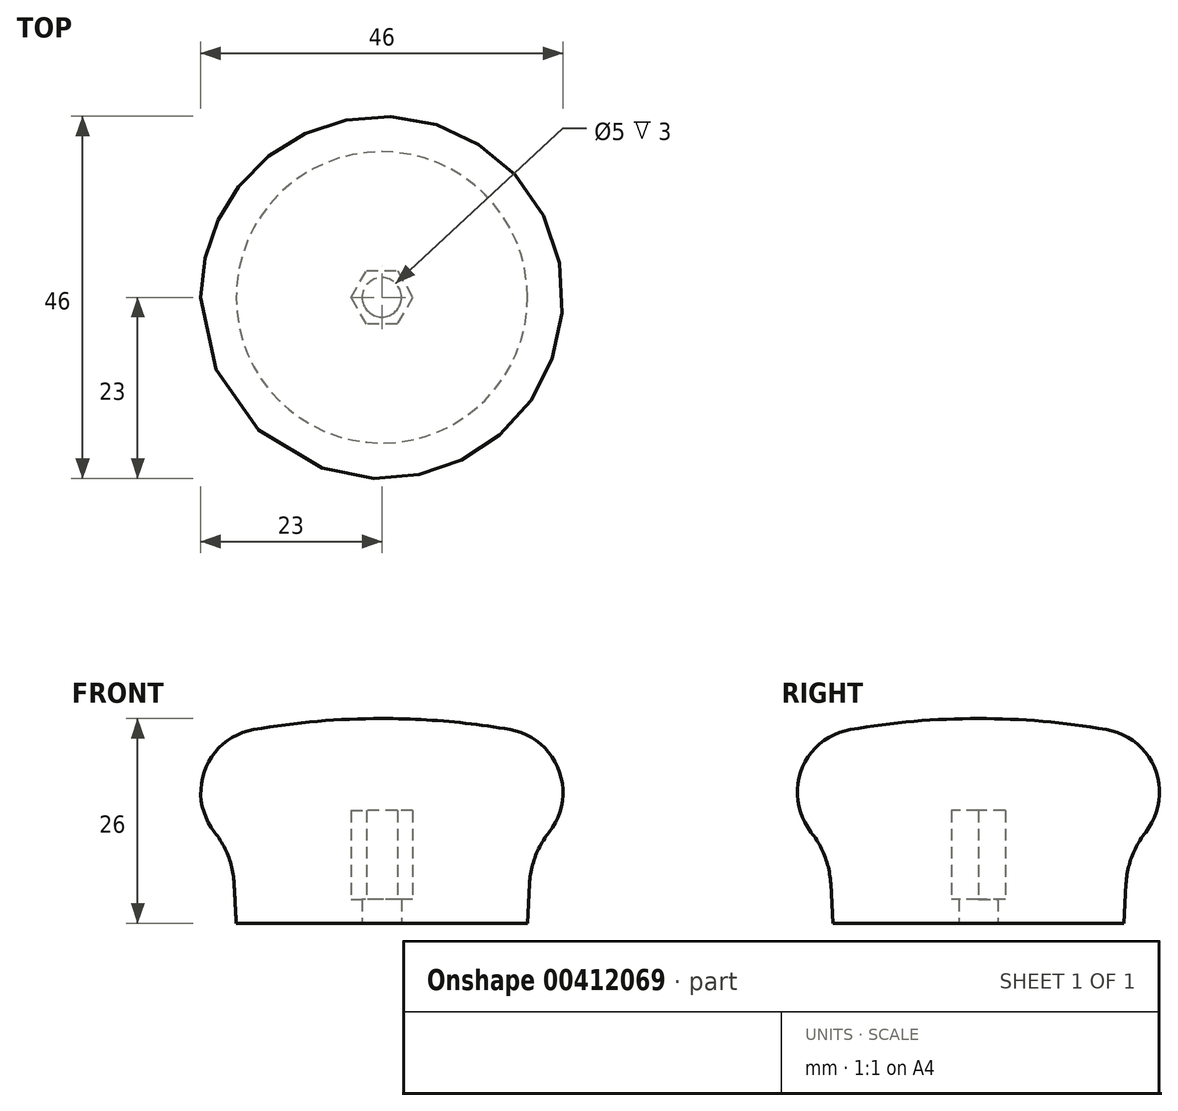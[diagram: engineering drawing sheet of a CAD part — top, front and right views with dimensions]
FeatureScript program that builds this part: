
annotation { "Feature Type Name" : "Feature", "Feature Type Description" : "" }
export const myFeature = defineFeature(function(context is Context, id is Id, definition is map)
    precondition{}
    {
        {
            var Q0;
            Q0=qCreatedBy(makeId("Front.planeOp"),FACE);
            var sketch = newSketch(context, id + "F0", { "sketchPlane" : qUnion([Q0])});
            skLineSegment(sketch, "E0", {"start": v(0, 0) * mm, "end": v(0, 26) * mm, "construction": true});
            skLineSegment(sketch, "E1.bottom", {"start": v(-23, 26) * mm, "end": v(23, 26) * mm, "construction": true});
            skLineSegment(sketch, "E1.top", {"start": v(-23, 0) * mm, "end": v(23, 0) * mm, "construction": true});
            skLineSegment(sketch, "E1.left", {"start": v(-23, 26) * mm, "end": v(-23, 0) * mm, "construction": true});
            skLineSegment(sketch, "E1.right", {"start": v(23, 26) * mm, "end": v(23, 0) * mm, "construction": true});
            skLineSegment(sketch, "E2", {"start": v(0, 26) * mm, "end": v(0, 10) * mm});
            skLineSegment(sketch, "E3", {"start": v(-2.5, 10) * mm, "end": v(-2.5, 0) * mm});
            skLineSegment(sketch, "E4", {"start": v(-2.5, 0) * mm, "end": v(-18.5, 0) * mm});
            skLineSegment(sketch, "E5", {"start": v(-18.5, 0) * mm, "end": v(-18.76, 5) * mm});
            skArc(sketch, "E6", {"start": v(0, 26) * mm, "mid": v(-8.16, 25.65) * mm, "end": v(-16.27, 24.6) * mm});
            skArc(sketch, "E7", {"start": v(-16.27, 24.6) * mm, "mid": v(-22.47, 19.5) * mm, "end": v(-21.24, 11.55) * mm});
            skArc(sketch, "E8", {"start": v(-18.76, 5) * mm, "mid": v(-19.5, 8.47) * mm, "end": v(-21.24, 11.55) * mm});
            skLineSegment(sketch, "E9.MirrorCS", {"start": v(2.5, 10) * mm, "end": v(2.5, 0) * mm});
            skLineSegment(sketch, "E10.MirrorCS", {"start": v(18.5, 0) * mm, "end": v(18.76, 5) * mm});
            skLineSegment(sketch, "E11.MirrorCS", {"start": v(2.5, 0) * mm, "end": v(18.5, 0) * mm});
            skArc(sketch, "E12.MirrorCS", {"start": v(18.76, 5) * mm, "mid": v(19.5, 8.47) * mm, "end": v(21.24, 11.55) * mm});
            skArc(sketch, "E13.MirrorCS", {"start": v(16.27, 24.6) * mm, "mid": v(22.47, 19.5) * mm, "end": v(21.24, 11.55) * mm});
            skArc(sketch, "E14.MirrorCS", {"start": v(0, 26) * mm, "mid": v(8.16, 25.65) * mm, "end": v(16.27, 24.6) * mm});
            skLineSegment(sketch, "E15", {"start": v(-23, 16.6) * mm, "end": v(23, 16.6) * mm, "construction": true});
            skLineSegment(sketch, "E16", {"start": v(-2.5, 10) * mm, "end": v(2.5, 10) * mm});
            skSolve(sketch);
        }
        {
            var Q0;
            {var subQ1=sQuery(id+"F0.wireOp",EDGE,"E2");Q0=makeQuery(id+"F0.imprint","IMPRINT",FACE,{"disambiguationData":[TD([[makeQuery(id+"F0.imprint","IMPRINT",EDGE,{"derivedFrom":subQ1}),-1.0]])]});}
            var Q1;
            Q1=sQuery(id+"F0.wireOp",EDGE,"E0");
            revolve(context, id + "F1", {"entities" : qUnion([Q0]), "axis" : qUnion([Q1]), "revolveType" : RevolveType.FULL});
        }
        {
            var Q0;
            Q0=qCreatedBy(makeId("Top.planeOp"),FACE);
            var sketch = newSketch(context, id + "F2", { "sketchPlane" : qUnion([Q0])});
            skCircle(sketch, "E17.cCircle", {"center": v(0, 0) * mm, "radius": 3.4 * mm, "construction": true});
            skLineSegment(sketch, "E17.0", {"start": v(1.96, -3.4) * mm, "end": v(-1.96, -3.4) * mm});
            skLineSegment(sketch, "E17.1", {"start": v(-1.96, -3.4) * mm, "end": v(-3.93, 0) * mm});
            skLineSegment(sketch, "E17.2", {"start": v(-3.93, 0) * mm, "end": v(-1.96, 3.4) * mm});
            skLineSegment(sketch, "E17.3", {"start": v(-1.96, 3.4) * mm, "end": v(1.96, 3.4) * mm});
            skLineSegment(sketch, "E17.4", {"start": v(1.96, 3.4) * mm, "end": v(3.93, 0) * mm});
            skLineSegment(sketch, "E17.5", {"start": v(3.93, 0) * mm, "end": v(1.96, -3.4) * mm});
            skPoint(sketch, "E17.0.midPoint", {"position": v(0, -3.4) * mm});
            skSolve(sketch);
        }
        {
            var Q0;
            Q0=makeQuery(id+"F2.imprint","IMPRINT",FACE,{"disambiguationData":[TD([[makeQuery(id+"F2.imprint","IMPRINT",EDGE,{"derivedFrom":sQuery(id+"F2.wireOp",EDGE,"E17.0")}),-1.0]])]});
            extrude(context, id + "F3", {"entities" : qUnion([Q0]), "operationType" : NewBodyOperationType.REMOVE, "depth" : (11.3 + 3) * mm, "hasSecondDirection" : true, "secondDirectionOppositeDirection" : false, "secondDirectionDepth" : 3 * mm});
        }
    });
